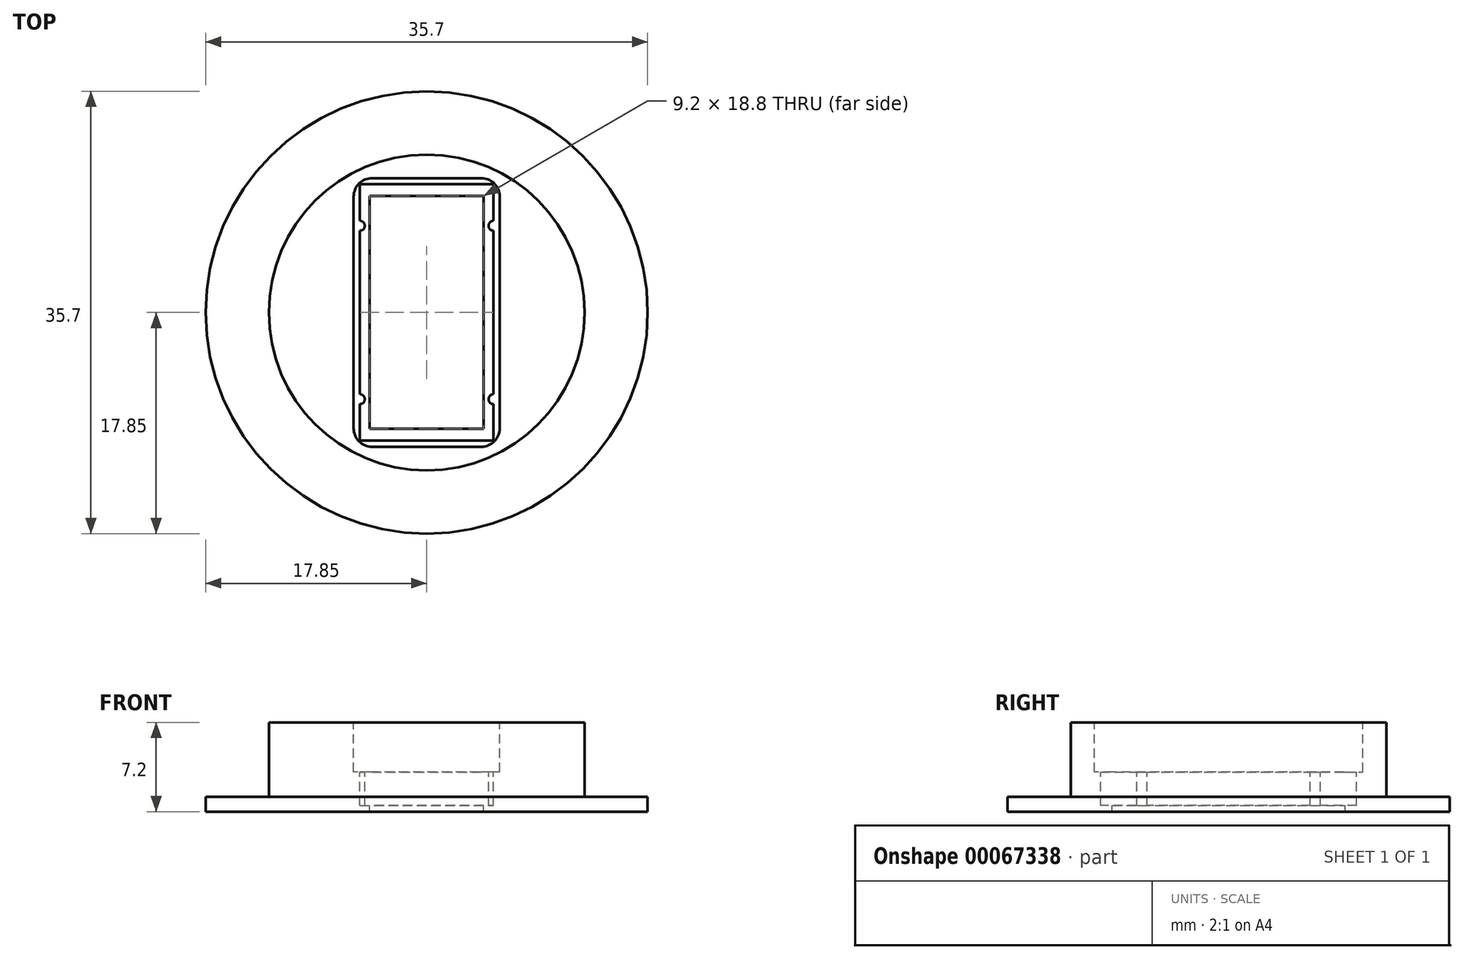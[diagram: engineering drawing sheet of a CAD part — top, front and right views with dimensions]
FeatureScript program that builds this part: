
annotation { "Feature Type Name" : "Feature", "Feature Type Description" : "" }
export const myFeature = defineFeature(function(context is Context, id is Id, definition is map)
    precondition{}
    {
        {
            var Q0;
            Q0=qCreatedBy(makeId("Top.planeOp"),FACE);
            var sketch = newSketch(context, id + "F0", { "sketchPlane" : qUnion([Q0])});
            skCircle(sketch, "E0", {"center": v(0, 0) * mm, "radius": 17.85 * mm});
            skSolve(sketch);
        }
        {
            var Q0;
            Q0 = qSketchRegion(id + "F0", true);
            extrude(context, id + "F1", {"entities" : qUnion([Q0]), "depth" : 1.2 * mm});
        }
        {
            var Q0;
            Q0=makeQuery(id+"F1.opExtrude","CAP_FACE",FACE,{"disambiguationData":[OSD([sQuery(id+"F0.wireOp",EDGE,"E0")])],"isStart":false});
            var sketch = newSketch(context, id + "F2", { "sketchPlane" : qUnion([Q0])});
            skCircle(sketch, "E1", {"center": v(0, 0) * mm, "radius": 12.75 * mm});
            skSolve(sketch);
        }
        {
            var Q0;
            Q0 = qSketchRegion(id + "F2", true);
            extrude(context, id + "F3", {"entities" : qUnion([Q0]), "operationType" : NewBodyOperationType.ADD, "depth" : 6 * mm});
        }
        {
            var Q0;
            Q0=makeQuery(id+"F3.opExtrude","CAP_FACE",FACE,{"disambiguationData":[OSD([sQuery(id+"F2.wireOp",EDGE,"E1")])],"isStart":false});
            var sketch = newSketch(context, id + "F4", { "sketchPlane" : qUnion([Q0])});
            skLineSegment(sketch, "E2.bottom", {"start": v(-4.6, 9.4) * mm, "end": v(4.6, 9.4) * mm});
            skLineSegment(sketch, "E2.top", {"start": v(-4.6, -9.4) * mm, "end": v(4.6, -9.4) * mm});
            skLineSegment(sketch, "E2.left", {"start": v(-4.6, 9.4) * mm, "end": v(-4.6, -9.4) * mm});
            skLineSegment(sketch, "E2.right", {"start": v(4.6, 9.4) * mm, "end": v(4.6, -9.4) * mm});
            skSolve(sketch);
        }
        {
            var Q0;
            Q0 = qSketchRegion(id + "F4", true);
            extrude(context, id + "F5", {"entities" : qUnion([Q0]), "operationType" : NewBodyOperationType.REMOVE, "endBound" : BoundingType.THROUGH_ALL, "oppositeDirection" : true, "depth" : 25 * mm});
        }
        {
            var Q0;
            Q0=makeQuery(id+"F3.opExtrude","CAP_FACE",FACE,{"disambiguationData":[OSD([sQuery(id+"F2.wireOp",EDGE,"E1")])],"isStart":false});
            var sketch = newSketch(context, id + "F6", { "sketchPlane" : qUnion([Q0])});
            skLineSegment(sketch, "E3.bottom", {"start": v(-5.4, 10.35) * mm, "end": v(5.4, 10.35) * mm});
            skLineSegment(sketch, "E3.top", {"start": v(-5.4, -10.35) * mm, "end": v(5.4, -10.35) * mm});
            skLineSegment(sketch, "E3.left", {"start": v(-5.4, 10.35) * mm, "end": v(-5.4, 7.4) * mm});
            skLineSegment(sketch, "E3.right", {"start": v(5.4, 10.35) * mm, "end": v(5.4, 7.4) * mm});
            skArc(sketch, "E4", {"start": v(5.4, 7.4) * mm, "mid": v(5, 7) * mm, "end": v(5.4, 6.6) * mm});
            skArc(sketch, "E5", {"start": v(5.4, -6.6) * mm, "mid": v(5, -7) * mm, "end": v(5.4, -7.4) * mm});
            skArc(sketch, "E6", {"start": v(-5.4, 6.6) * mm, "mid": v(-5, 7) * mm, "end": v(-5.4, 7.4) * mm});
            skArc(sketch, "E7", {"start": v(-5.4, -7.4) * mm, "mid": v(-5, -7) * mm, "end": v(-5.4, -6.6) * mm});
            skLineSegment(sketch, "E8.trimOffspring", {"start": v(5.4, 6.6) * mm, "end": v(5.4, -6.6) * mm});
            skLineSegment(sketch, "E9.trimOffspring", {"start": v(-5.4, 6.6) * mm, "end": v(-5.4, -6.6) * mm});
            skLineSegment(sketch, "E10.trimOffspring", {"start": v(-5.4, -7.4) * mm, "end": v(-5.4, -10.35) * mm});
            skLineSegment(sketch, "E11.trimOffspring", {"start": v(5.4, -7.4) * mm, "end": v(5.4, -10.35) * mm});
            skSolve(sketch);
        }
        {
            var Q0;
            Q0 = qSketchRegion(id + "F6", true);
            extrude(context, id + "F7", {"entities" : qUnion([Q0]), "operationType" : NewBodyOperationType.REMOVE, "oppositeDirection" : true, "depth" : 6.7 * mm});
        }
        {
            var Q0;
            Q0=makeQuery(id+"F3.opExtrude","CAP_FACE",FACE,{"disambiguationData":[OSD([sQuery(id+"F2.wireOp",EDGE,"E1")])],"isStart":false});
            var sketch = newSketch(context, id + "F8", { "sketchPlane" : qUnion([Q0])});
            skLineSegment(sketch, "E12.bottom", {"start": v(-4.4, 10.85) * mm, "end": v(4.4, 10.85) * mm});
            skLineSegment(sketch, "E12.top", {"start": v(-4.4, -10.85) * mm, "end": v(4.4, -10.85) * mm});
            skLineSegment(sketch, "E12.left", {"start": v(-5.9, 9.35) * mm, "end": v(-5.9, -9.35) * mm});
            skLineSegment(sketch, "E12.right", {"start": v(5.9, 9.35) * mm, "end": v(5.9, -9.35) * mm});
            skPoint(sketch, "E13.visualSharp", {"position": v(-5.9, 10.85) * mm});
            skArc(sketch, "E13.filletArc", {"start": v(-4.4, 10.85) * mm, "mid": v(-5.46, 10.41) * mm, "end": v(-5.9, 9.35) * mm});
            skPoint(sketch, "E14.visualSharp", {"position": v(5.9, 10.85) * mm});
            skArc(sketch, "E14.filletArc", {"start": v(5.9, 9.35) * mm, "mid": v(5.46, 10.41) * mm, "end": v(4.4, 10.85) * mm});
            skPoint(sketch, "E15.visualSharp", {"position": v(5.9, -10.85) * mm});
            skArc(sketch, "E15.filletArc", {"start": v(4.4, -10.85) * mm, "mid": v(5.46, -10.41) * mm, "end": v(5.9, -9.35) * mm});
            skPoint(sketch, "E16.visualSharp", {"position": v(-5.9, -10.85) * mm});
            skArc(sketch, "E16.filletArc", {"start": v(-5.9, -9.35) * mm, "mid": v(-5.46, -10.41) * mm, "end": v(-4.4, -10.85) * mm});
            skSolve(sketch);
        }
        {
            var Q0;
            Q0 = qSketchRegion(id + "F8", true);
            extrude(context, id + "F9", {"entities" : qUnion([Q0]), "operationType" : NewBodyOperationType.REMOVE, "oppositeDirection" : true, "depth" : 4 * mm});
        }
    });
